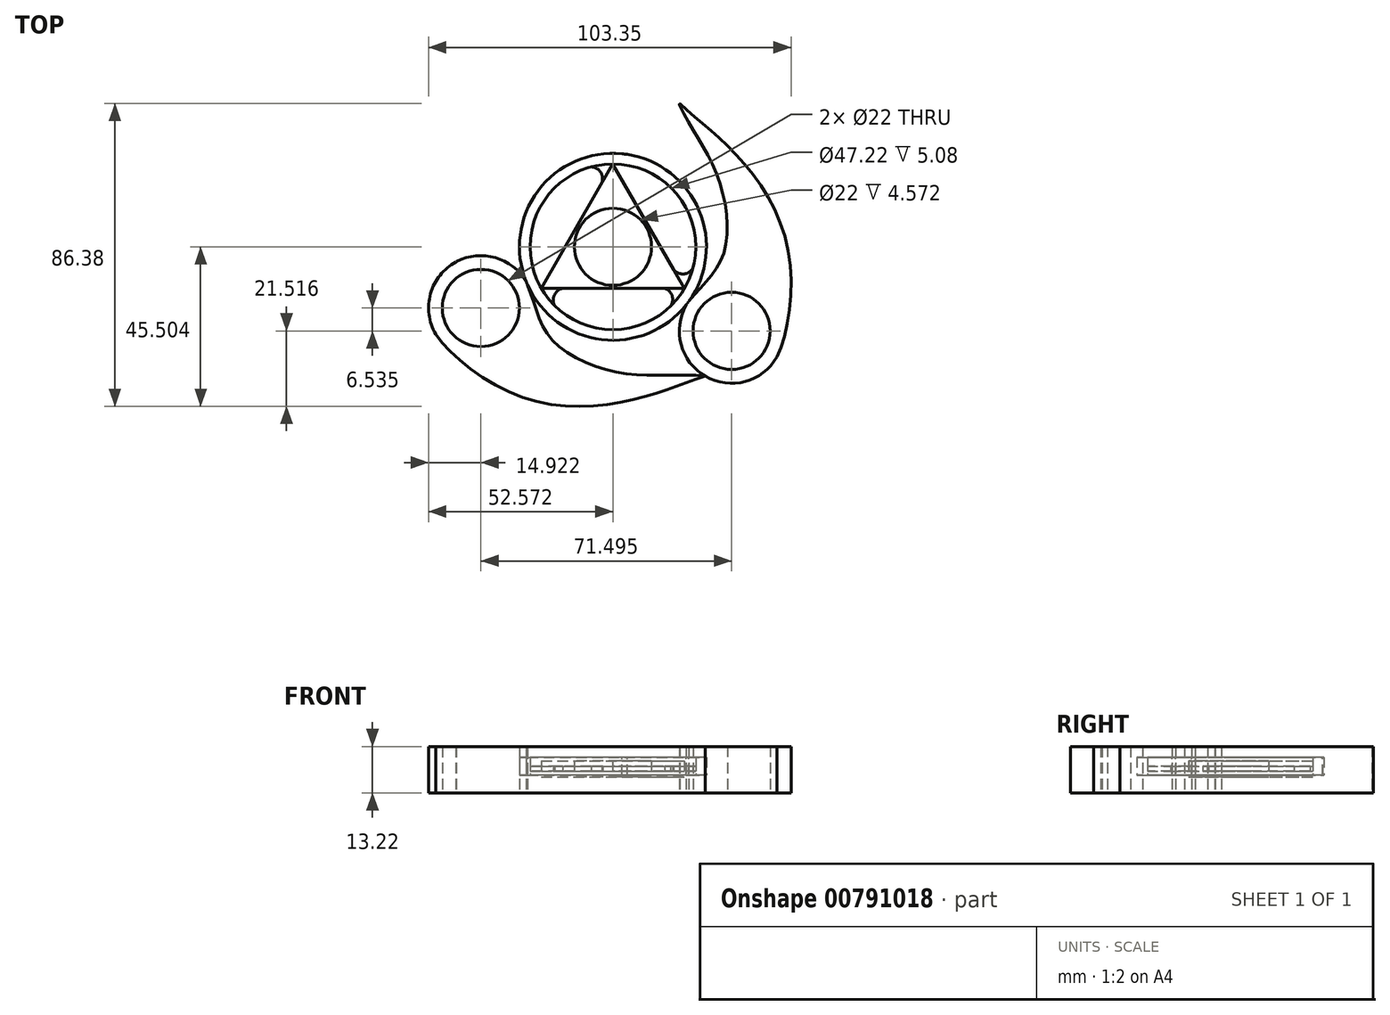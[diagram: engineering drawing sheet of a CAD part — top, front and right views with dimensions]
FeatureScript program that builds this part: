
annotation { "Feature Type Name" : "Feature", "Feature Type Description" : "" }
export const myFeature = defineFeature(function(context is Context, id is Id, definition is map)
    precondition{}
    {
        {
            var Q0;
            Q0=qCreatedBy(makeId("Top.planeOp"),FACE);
            var sketch = newSketch(context, id + "F0", { "sketchPlane" : qUnion([Q0])});
            skCircle(sketch, "E0", {"center": v(-0.22, 0.08) * mm, "radius": 11 * mm});
            skLineSegment(sketch, "E1", {"start": v(9.05, 7.44) * mm, "end": v(20.18, -11.72) * mm});
            skLineSegment(sketch, "E2", {"start": v(-20.63, -11.78) * mm, "end": v(20.18, -11.72) * mm});
            skLineSegment(sketch, "E3.MirrorCS", {"start": v(-20.65, -11.74) * mm, "end": v(-0.3, 23.7) * mm});
            skLineSegment(sketch, "E4.MirrorCS", {"start": v(9.05, 7.44) * mm, "end": v(-0.3, 23.7) * mm});
            skCircle(sketch, "E5", {"center": v(-0.22, 0.08) * mm, "radius": 23.61 * mm});
            skCircle(sketch, "E6", {"center": v(-0.22, 0.08) * mm, "radius": 26.66 * mm});
            skArc(sketch, "E7", {"start": v(5.82, 22.91) * mm, "mid": v(3.13, 21.43) * mm, "end": v(2.76, 18.38) * mm});
            skArc(sketch, "E8.MirrorCS", {"start": v(22.57, -6.1) * mm, "mid": v(19.94, -7.67) * mm, "end": v(17.12, -6.46) * mm});
            skArc(sketch, "E9.MirrorCS", {"start": v(16.15, -16.93) * mm, "mid": v(16.65, -13.9) * mm, "end": v(14.49, -11.73) * mm});
            skArc(sketch, "E10.MirrorCS", {"start": v(-16.8, -16.73) * mm, "mid": v(-16.91, -13.66) * mm, "end": v(-14.49, -11.77) * mm});
            skArc(sketch, "E11.MirrorCS", {"start": v(-6.44, 22.86) * mm, "mid": v(-3.75, 21.38) * mm, "end": v(-3.38, 18.33) * mm});
            skArc(sketch, "E12.MirrorCS", {"start": v(-23.03, -6) * mm, "mid": v(-20.4, -7.6) * mm, "end": v(-17.58, -6.4) * mm});
            skCircle(sketch, "E13", {"center": v(33.63, -23.9) * mm, "radius": 11 * mm});
            skArc(sketch, "E14", {"start": v(20.7, -16.44) * mm, "mid": v(26.17, -36.83) * mm, "end": v(46.55, -31.37) * mm});
            skLineSegment(sketch, "E15.0", {"start": v(-14.49, -11.77) * mm, "end": v(-17.2, -16.5) * mm, "construction": true});
            skLineSegment(sketch, "E15.1", {"start": v(-17.2, -16.5) * mm, "end": v(-16.8, -16.73) * mm, "construction": true});
            skLineSegment(sketch, "E16.0", {"start": v(20.7, -16.44) * mm, "end": v(46.55, -31.37) * mm, "construction": true});
            skCircle(sketch, "E17", {"center": v(3.89, 41.35) * mm, "radius": 11 * mm});
            skArc(sketch, "E18", {"start": v(3.89, 26.43) * mm, "mid": v(18.81, 41.35) * mm, "end": v(3.89, 56.28) * mm});
            skLineSegment(sketch, "E19.0", {"start": v(3.89, 26.43) * mm, "end": v(3.89, 56.28) * mm, "construction": true});
            skCircle(sketch, "E20", {"center": v(-37.86, -17.37) * mm, "radius": 11 * mm});
            skArc(sketch, "E21", {"start": v(-24.94, -9.9) * mm, "mid": v(-45.32, -4.44) * mm, "end": v(-50.79, -24.83) * mm});
            skFitSpline(sketch, "E22", {"points": [v(-50.79, -24.83) * mm, v(-25.17, -43.1) * mm, v(6.96, -43.15) * mm, v(26.17, -36.83) * mm], "startDerivative": vector(35.78, -52.34) * mm, "endDerivative": vector(62.37, 18.62) * mm});
            skFitSpline(sketch, "E23", {"points": [v(26.17, -36.83) * mm, v(3.37, -36.05) * mm, v(-18, -25.96) * mm, v(-24.94, -9.9) * mm], "startDerivative": vector(-64.96, 7.81) * mm, "endDerivative": vector(-24.44, 54.35) * mm});
            skLineSegment(sketch, "E24.0", {"start": v(-24.94, -9.9) * mm, "end": v(-50.79, -24.83) * mm, "construction": true});
            skFitSpline(sketch, "E25", {"points": [v(46.55, -31.37) * mm, v(49.57, -0.05) * mm, v(33.54, 27.8) * mm, v(18.47, 41.27) * mm], "startDerivative": vector(27.44, 57.15) * mm, "endDerivative": vector(-47.31, 44.7) * mm});
            skFitSpline(sketch, "E26", {"points": [v(18.47, 41.27) * mm, v(29.19, 21.14) * mm, v(31.14, -2.4) * mm, v(20.7, -16.44) * mm], "startDerivative": vector(25.72, -60.17) * mm, "endDerivative": vector(-34.85, -48.34) * mm});
            skFitSpline(sketch, "E27", {"points": [v(3.89, 56.28) * mm, v(-24.74, 43.23) * mm, v(-40.85, 15.42) * mm, v(-44.98, -4.37) * mm], "startDerivative": vector(-63.22, -4.81) * mm, "endDerivative": vector(-15.06, -63.32) * mm});
            skFitSpline(sketch, "E28", {"points": [v(-44.98, -4.37) * mm, v(-32.9, 14.98) * mm, v(-13.49, 28.44) * mm, v(3.89, 26.43) * mm], "startDerivative": vector(39.25, 52.35) * mm, "endDerivative": vector(59.3, -6) * mm});
            skSolve(sketch);
        }
        {
            var Q0;
            Q0=makeQuery(id+"F0.imprint","IMPRINT",FACE,{"disambiguationData":[TD([[makeQuery(id+"F0.imprint","IMPRINT",EDGE,{"derivedFrom":sQuery(id+"F0.wireOp",EDGE,"E17")}),-1.0]])]});
            var Q1;
            Q1=makeQuery(id+"F0.imprint","IMPRINT",FACE,{"disambiguationData":[TD([[makeQuery(id+"F0.imprint","IMPRINT",EDGE,{"derivedFrom":sQuery(id+"F0.wireOp",EDGE,"E13")}),-1.0]])]});
            var Q2;
            Q2=makeQuery(id+"F0.imprint","IMPRINT",FACE,{"disambiguationData":[TD([[makeQuery(id+"F0.imprint","IMPRINT",EDGE,{"derivedFrom":sQuery(id+"F0.wireOp",EDGE,"E20")}),-1.0]])]});
            extrude(context, id + "F1", {"entities" : qUnion([Q0, Q1, Q2]), "depth" : 13.2 * mm, "offsetDistance" : 25.4 * mm});
        }
        {
            var Q0;
            {var subQ5=sQuery(id+"F0.wireOp",EDGE,"E5");var subQ8=sQuery(id+"F0.wireOp",EDGE,"E3.MirrorCS");var subQ14=makeQuery(id+"F0.imprint","INTERSECT",VERTEX,{"derivedFrom":[subQ8,subQ5]});Q0=makeQuery(id+"F0.imprint","IMPRINT",FACE,{"disambiguationData":[TD([[makeQuery(id+"F0.imprint","IMPRINT",EDGE,{"disambiguationData":[TD([[subQ14,1.0]])],"derivedFrom":subQ5}),-1.0]])]});}
            extrude(context, id + "F2", {"entities" : qUnion([Q0]), "depth" : 10.16 * mm, "offsetDistance" : 25.4 * mm});
        }
        {
            var Q0;
            Q0=makeQuery(id+"F0.imprint","IMPRINT",FACE,{"disambiguationData":[TD([[makeQuery(id+"F0.imprint","IMPRINT",EDGE,{"derivedFrom":sQuery(id+"F0.wireOp",EDGE,"E0")}),-1.0]])]});
            extrude(context, id + "F3", {"entities" : qUnion([Q0]), "depth" : 9.14 * mm, "offsetDistance" : 25.4 * mm});
        }
        {
            var Q0;
            {var subQ3=sQuery(id+"F0.wireOp",EDGE,"E7");Q0=makeQuery(id+"F0.imprint","IMPRINT",FACE,{"disambiguationData":[TD([[makeQuery(id+"F0.imprint","IMPRINT",EDGE,{"derivedFrom":subQ3}),-1.0]])]});}
            var Q1;
            {var subQ3=sQuery(id+"F0.wireOp",EDGE,"E11.MirrorCS");Q1=makeQuery(id+"F0.imprint","IMPRINT",FACE,{"disambiguationData":[TD([[makeQuery(id+"F0.imprint","IMPRINT",EDGE,{"derivedFrom":subQ3}),1.0]])]});}
            var Q2;
            {var subQ3=sQuery(id+"F0.wireOp",EDGE,"E12.MirrorCS");Q2=makeQuery(id+"F0.imprint","IMPRINT",FACE,{"disambiguationData":[TD([[makeQuery(id+"F0.imprint","IMPRINT",EDGE,{"derivedFrom":subQ3}),-1.0]])]});}
            var Q3;
            {var subQ3=sQuery(id+"F0.wireOp",EDGE,"E10.MirrorCS");Q3=makeQuery(id+"F0.imprint","IMPRINT",FACE,{"disambiguationData":[TD([[makeQuery(id+"F0.imprint","IMPRINT",EDGE,{"derivedFrom":subQ3}),1.0]])]});}
            var Q4;
            {var subQ0=sQuery(id+"F0.wireOp",EDGE,"E8.MirrorCS");Q4=makeQuery(id+"F0.imprint","IMPRINT",FACE,{"disambiguationData":[TD([[makeQuery(id+"F0.imprint","IMPRINT",EDGE,{"derivedFrom":subQ0}),1.0]])]});}
            extrude(context, id + "F4", {"entities" : qUnion([Q0, Q1, Q2, Q3, Q4]), "depth" : 7.62 * mm, "offsetDistance" : 25.4 * mm});
        }
        {
            var Q0;
            {var subQ5=sQuery(id+"F0.wireOp",EDGE,"E5");var subQ8=sQuery(id+"F0.wireOp",EDGE,"E3.MirrorCS");var subQ14=makeQuery(id+"F0.imprint","INTERSECT",VERTEX,{"derivedFrom":[subQ8,subQ5]});Q0=makeQuery(id+"F0.imprint","IMPRINT",FACE,{"disambiguationData":[TD([[makeQuery(id+"F0.imprint","IMPRINT",EDGE,{"disambiguationData":[TD([[subQ14,1.0]])],"derivedFrom":subQ5}),-1.0]])]});}
            extrude(context, id + "F5", {"entities" : qUnion([Q0]), "operationType" : NewBodyOperationType.REMOVE, "depth" : 5.08 * mm, "offsetDistance" : 25.4 * mm});
        }
        {
            var Q0;
            Q0=makeQuery(id+"F0.imprint","IMPRINT",FACE,{"disambiguationData":[TD([[makeQuery(id+"F0.imprint","IMPRINT",EDGE,{"derivedFrom":sQuery(id+"F0.wireOp",EDGE,"E0")}),-1.0]])]});
            extrude(context, id + "F6", {"entities" : qUnion([Q0]), "operationType" : NewBodyOperationType.REMOVE, "depth" : 4.57 * mm, "offsetDistance" : 25.4 * mm});
        }
        {
            var Q0;
            {var subQ3=sQuery(id+"F0.wireOp",EDGE,"E10.MirrorCS");Q0=makeQuery(id+"F0.imprint","IMPRINT",FACE,{"disambiguationData":[TD([[makeQuery(id+"F0.imprint","IMPRINT",EDGE,{"derivedFrom":subQ3}),1.0]])]});}
            var Q1;
            {var subQ3=sQuery(id+"F0.wireOp",EDGE,"E12.MirrorCS");Q1=makeQuery(id+"F0.imprint","IMPRINT",FACE,{"disambiguationData":[TD([[makeQuery(id+"F0.imprint","IMPRINT",EDGE,{"derivedFrom":subQ3}),-1.0]])]});}
            var Q2;
            {var subQ0=sQuery(id+"F0.wireOp",EDGE,"E8.MirrorCS");Q2=makeQuery(id+"F0.imprint","IMPRINT",FACE,{"disambiguationData":[TD([[makeQuery(id+"F0.imprint","IMPRINT",EDGE,{"derivedFrom":subQ0}),1.0]])]});}
            var Q3;
            {var subQ3=sQuery(id+"F0.wireOp",EDGE,"E11.MirrorCS");Q3=makeQuery(id+"F0.imprint","IMPRINT",FACE,{"disambiguationData":[TD([[makeQuery(id+"F0.imprint","IMPRINT",EDGE,{"derivedFrom":subQ3}),1.0]])]});}
            var Q4;
            {var subQ3=sQuery(id+"F0.wireOp",EDGE,"E7");Q4=makeQuery(id+"F0.imprint","IMPRINT",FACE,{"disambiguationData":[TD([[makeQuery(id+"F0.imprint","IMPRINT",EDGE,{"derivedFrom":subQ3}),-1.0]])]});}
            extrude(context, id + "F7", {"entities" : qUnion([Q0, Q1, Q2, Q3, Q4]), "operationType" : NewBodyOperationType.REMOVE, "depth" : 6.15 * mm, "offsetDistance" : 25.4 * mm});
        }
        {
            var Q0;
            Q0=makeQuery(id+"F1.opExtrude","SWEPT_BODY",BODY,{"disambiguationData":[OSD([sQuery(id+"F0.wireOp",EDGE,"E6"),sQuery(id+"F0.wireOp",EDGE,"E21"),sQuery(id+"F0.wireOp",EDGE,"E25"),sQuery(id+"F0.wireOp",EDGE,"E26"),sQuery(id+"F0.wireOp",EDGE,"E17"),sQuery(id+"F0.wireOp",EDGE,"E18"),sQuery(id+"F0.wireOp",EDGE,"E27"),sQuery(id+"F0.wireOp",EDGE,"E28")])]});
            transform(context, id + "F8", {"entities" : qUnion([Q0]), "transformType" : TransformType.TRANSLATION_3D, "dx" : 0 * mm, "dy" : 0 * mm, "dz" : 0 * mm, "makeCopy" : false});
        }
    });
